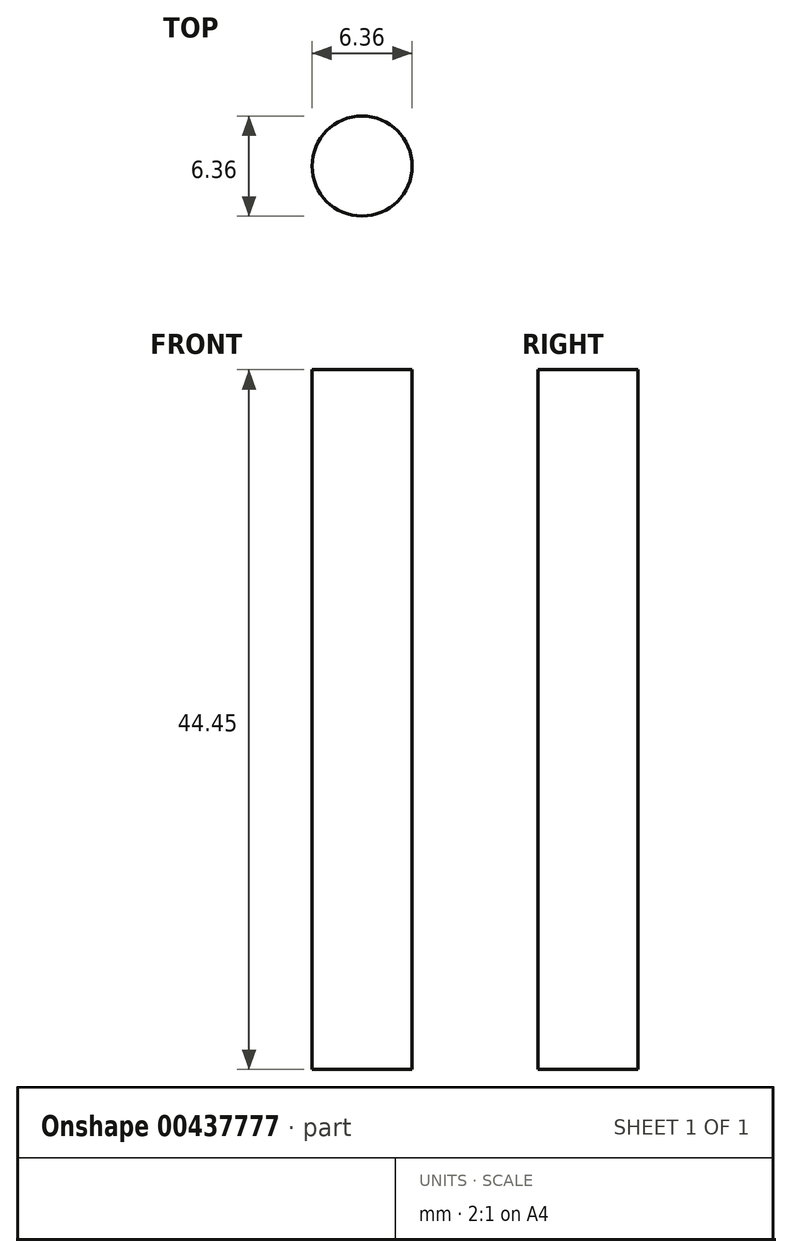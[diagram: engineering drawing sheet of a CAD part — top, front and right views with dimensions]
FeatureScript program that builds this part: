
annotation { "Feature Type Name" : "Feature", "Feature Type Description" : "" }
export const myFeature = defineFeature(function(context is Context, id is Id, definition is map)
    precondition{}
    {
        {
            var Q0;
            Q0=qCreatedBy(makeId("Top.planeOp"),FACE);
            var sketch = newSketch(context, id + "F0", { "sketchPlane" : qUnion([Q0])});
            skCircle(sketch, "E0", {"center": v(0, 0) * mm, "radius": 3.18 * mm});
            skSolve(sketch);
        }
        {
            var Q0;
            Q0 = qSketchRegion(id + "F0", true);
            extrude(context, id + "F1", {"entities" : qUnion([Q0]), "depth" : 44.45 * mm});
        }
    });
